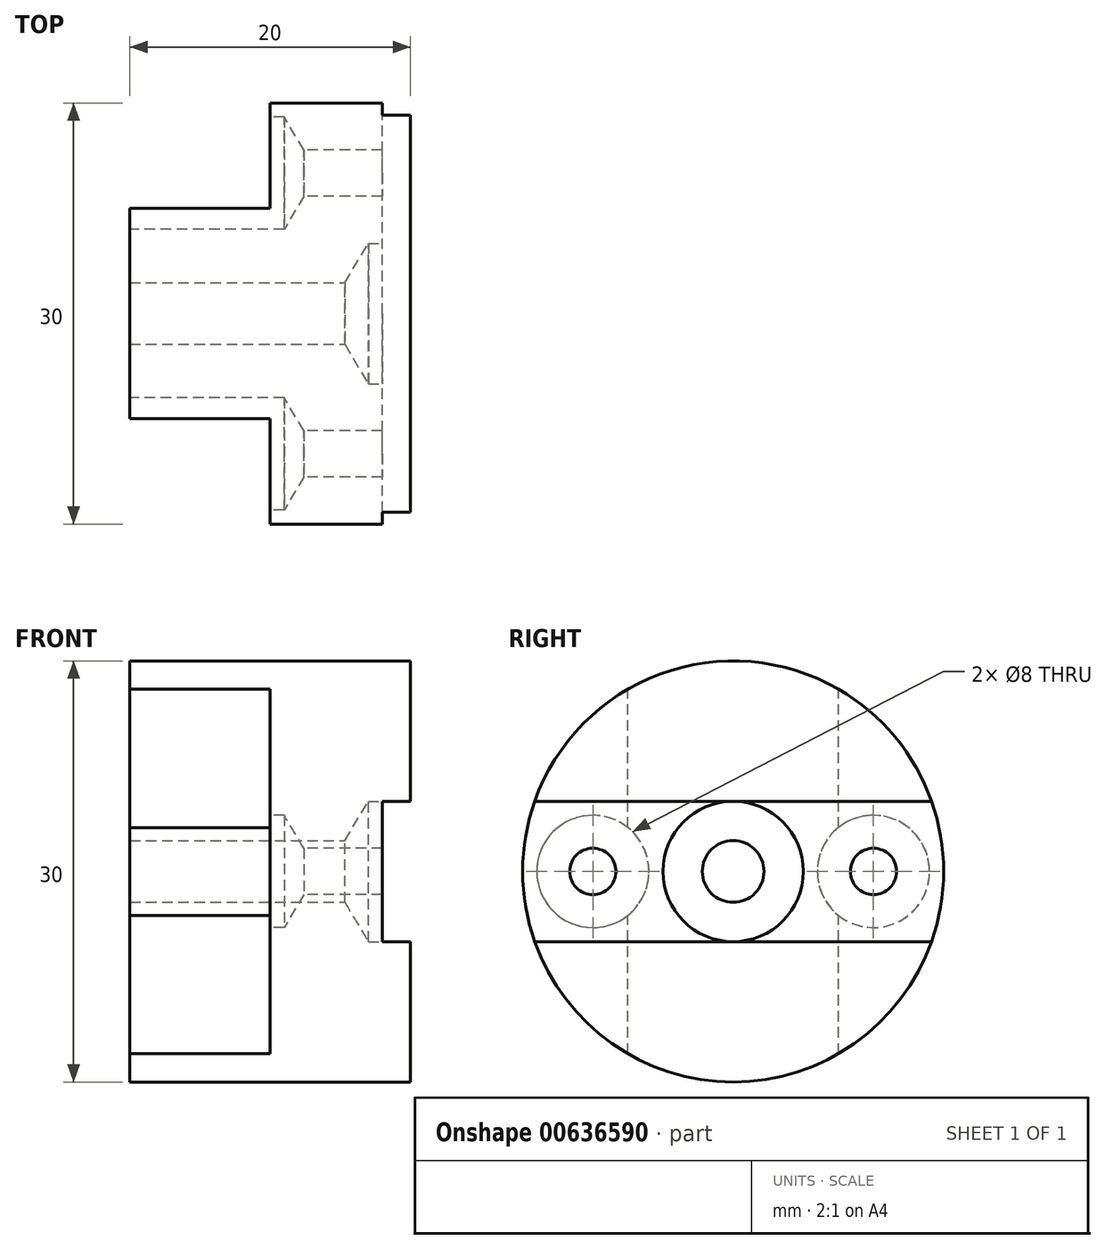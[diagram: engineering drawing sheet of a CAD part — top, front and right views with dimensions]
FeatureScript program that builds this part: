
annotation { "Feature Type Name" : "Feature", "Feature Type Description" : "" }
export const myFeature = defineFeature(function(context is Context, id is Id, definition is map)
    precondition{}
    {
        {
            var Q0;
            Q0=qCreatedBy(makeId("Right.planeOp"),FACE);
            var sketch = newSketch(context, id + "F0", { "sketchPlane" : qUnion([Q0])});
            skCircle(sketch, "E0", {"center": v(0, 0) * mm, "radius": 15 * mm});
            skSolve(sketch);
        }
        {
            var Q0;
            Q0=makeQuery(id+"F0.imprint","IMPRINT",FACE,{"disambiguationData":[TD([[makeQuery(id+"F0.imprint","IMPRINT",EDGE,{"derivedFrom":sQuery(id+"F0.wireOp",EDGE,"E0")}),1.0]])]});
            extrude(context, id + "F1", {"entities" : qUnion([Q0]), "depth" : 20 * mm, "offsetDistance" : 25 * mm});
        }
        {
            var Q0;
            Q0=makeQuery(id+"F1.opExtrude","CAP_FACE",FACE,{"disambiguationData":[OSD([sQuery(id+"F0.wireOp",EDGE,"E0"),sQuery(id+"F0.wireOp",EDGE,"ugKhpiQA-20zx-WtLt-apDM-YFJ7EFN9A7Jh"),sQuery(id+"F0.wireOp",EDGE,"ICKhDrLO-E7QP-m0pU-s6IP-EmB2PJC27SfZ")])],"isStart":true});
            var sketch = newSketch(context, id + "F2", { "sketchPlane" : qUnion([Q0])});
            skArc(sketch, "E1", {"start": v(-7.5, 13) * mm, "mid": v(-15, 0) * mm, "end": v(-7.5, -13) * mm});
            skLineSegment(sketch, "E2", {"start": v(0, -15) * mm, "end": v(0, 15) * mm, "construction": true});
            skLineSegment(sketch, "E3.0", {"start": v(-7.5, -13) * mm, "end": v(-7.5, 13) * mm});
            skLineSegment(sketch, "E4.MirrorCS", {"start": v(7.5, -13) * mm, "end": v(7.5, 13) * mm});
            skArc(sketch, "E5.trimOffspring", {"start": v(7.5, -13) * mm, "mid": v(15, 0) * mm, "end": v(7.5, 13) * mm});
            skSolve(sketch);
        }
        {
            var Q0;
            Q0 = qSketchRegion(id + "F2", true);
            extrude(context, id + "F3", {"entities" : qUnion([Q0]), "operationType" : NewBodyOperationType.REMOVE, "oppositeDirection" : true, "depth" : 10 * mm, "offsetDistance" : 25 * mm});
        }
        {
            var Q0;
            Q0=makeQuery(id+"F1.opExtrude","CAP_FACE",FACE,{"disambiguationData":[OSD([sQuery(id+"F0.wireOp",EDGE,"E0")])],"isStart":false});
            var sketch = newSketch(context, id + "F4", { "sketchPlane" : qUnion([Q0])});
            skPoint(sketch, "E6", {"position": v(0, 0) * mm});
            skPoint(sketch, "E7", {"position": v(9.5, 0) * mm});
            skPoint(sketch, "E8", {"position": v(-9.5, 0) * mm});
            skSolve(sketch);
        }
        {
            var Q0;
            Q0=sQuery(id+"F4.wireOp",VERTEX,"E6");
            var Q1;
            Q1=makeQuery(id+"F1.opExtrude","SWEPT_BODY",BODY,{"disambiguationData":[OSD([sQuery(id+"F0.wireOp",EDGE,"E0")])]});
            hole(context, id + "F5", {"style" : HoleStyle.SIMPLE, "endStyle" : HoleEndStyle.THROUGH, "standardTappedOrClearance" : lookupTablePath({ "standard" : "ISO", "fit" : "Normal", "size" : "M4", "type" : "Clearance" }), "standardBlindInLast" : lookupTablePath({ "fit" : "Standard", "standard" : "ISO", "size" : "M4", "type" : "Clearance" }), "holeDiameter" : 4.4 * mm, "majorDiameter" : 4 * mm, "isTappedThrough" : true, "tappedDepth" : 5 * mm, "tapClearance" : 3, "locations" : qUnion([Q0]), "scope" : qUnion([Q1])});
        }
        {
            var Q0;
            Q0=makeQuery(id+"F3.boolean.opBoolean","COPY",FACE,{"derivedFrom":makeQuery(id+"F3.opExtrude","CAP_FACE",FACE,{"disambiguationData":[OSD([sQuery(id+"F2.wireOp",EDGE,"E1"),sQuery(id+"F2.wireOp",EDGE,"E3.0")])],"isStart":false})});
            var sketch = newSketch(context, id + "F6", { "sketchPlane" : qUnion([Q0])});
            skPoint(sketch, "E9", {"position": v(-10, 0) * mm});
            skPoint(sketch, "E10", {"position": v(10, 0) * mm});
            skSolve(sketch);
        }
        {
            var Q0;
            Q0=sQuery(id+"F6.wireOp",VERTEX,"E9");
            var Q1;
            Q1=sQuery(id+"F6.wireOp",VERTEX,"E10");
            var Q2;
            Q2=makeQuery(id+"F1.opExtrude","SWEPT_BODY",BODY,{"disambiguationData":[OSD([sQuery(id+"F0.wireOp",EDGE,"E0")])]});
            hole(context, id + "F7", {"style" : HoleStyle.C_SINK, "endStyle" : HoleEndStyle.THROUGH, "standardTappedOrClearance" : lookupTablePath({ "standard" : "ISO", "fit" : "Normal", "size" : "M3", "type" : "Clearance" }), "standardBlindInLast" : lookupTablePath({ "fit" : "Standard", "standard" : "ISO", "size" : "M3", "type" : "Clearance" }), "holeDiameter" : 3.3 * mm, "cSinkDiameter" : 6.72 * mm, "cSinkAngle" : 90 * degree, "majorDiameter" : 3 * mm, "isTappedThrough" : true, "tappedDepth" : 5 * mm, "tapClearance" : 3, "locations" : qUnion([Q0, Q1]), "scope" : qUnion([Q2])});
        }
        {
            var Q0;
            Q0=makeQuery(id+"F1.opExtrude","CAP_FACE",FACE,{"disambiguationData":[OSD([sQuery(id+"F0.wireOp",EDGE,"E0")])],"isStart":true});
            var sketch = newSketch(context, id + "F8", { "sketchPlane" : qUnion([Q0])});
            skPoint(sketch, "E11", {"position": v(-10, 0) * mm});
            skPoint(sketch, "E12", {"position": v(10, 0) * mm});
            skSolve(sketch);
        }
        {
            var Q0;
            Q0=sQuery(id+"F8.wireOp",VERTEX,"E11");
            var Q1;
            Q1=sQuery(id+"F8.wireOp",VERTEX,"E12");
            var Q2;
            Q2=makeQuery(id+"F1.opExtrude","SWEPT_BODY",BODY,{"disambiguationData":[OSD([sQuery(id+"F0.wireOp",EDGE,"E0")])]});
            hole(context, id + "F9", {"style" : HoleStyle.SIMPLE, "endStyle" : HoleEndStyle.BLIND, "holeDiameter" : 8 * mm, "majorDiameter" : 3 * mm, "holeDepth" : 1 * mm, "isTappedThrough" : true, "tappedDepth" : 5 * mm, "tapClearance" : 3, "locations" : qUnion([Q0, Q1]), "scope" : qUnion([Q2])});
        }
        {
            var Q0;
            Q0=sQuery(id+"F4.wireOp",VERTEX,"E6");
            var Q1;
            Q1=makeQuery(id+"F1.opExtrude","SWEPT_BODY",BODY,{"disambiguationData":[OSD([sQuery(id+"F0.wireOp",EDGE,"E0")])]});
            hole(context, id + "F10", {"style" : HoleStyle.SIMPLE, "endStyle" : HoleEndStyle.BLIND, "holeDiameter" : 10 * mm, "majorDiameter" : 5 * mm, "holeDepth" : 3 * mm, "isTappedThrough" : true, "tappedDepth" : 5 * mm, "tapClearance" : 3, "locations" : qUnion([Q0]), "scope" : qUnion([Q1])});
        }
        {
            var Q0;
            Q0=makeQuery(id+"F1.opExtrude","CAP_FACE",FACE,{"disambiguationData":[OSD([sQuery(id+"F0.wireOp",EDGE,"E0")])],"isStart":false});
            var sketch = newSketch(context, id + "F11", { "sketchPlane" : qUnion([Q0])});
            skArc(sketch, "E13", {"start": v(15, -5) * mm, "mid": v(20, 0) * mm, "end": v(15, 5) * mm});
            skArc(sketch, "E14", {"start": v(-15, 5) * mm, "mid": v(-20, 0) * mm, "end": v(-15, -5) * mm});
            skLineSegment(sketch, "E15", {"start": v(-15, -5) * mm, "end": v(15, -5) * mm});
            skLineSegment(sketch, "E16", {"start": v(-15, 5) * mm, "end": v(15, 5) * mm});
            skSolve(sketch);
        }
        {
            var Q0;
            Q0 = qSketchRegion(id + "F11", true);
            extrude(context, id + "F12", {"entities" : qUnion([Q0]), "operationType" : NewBodyOperationType.REMOVE, "oppositeDirection" : true, "depth" : 2 * mm, "offsetDistance" : 25 * mm});
        }
    });
